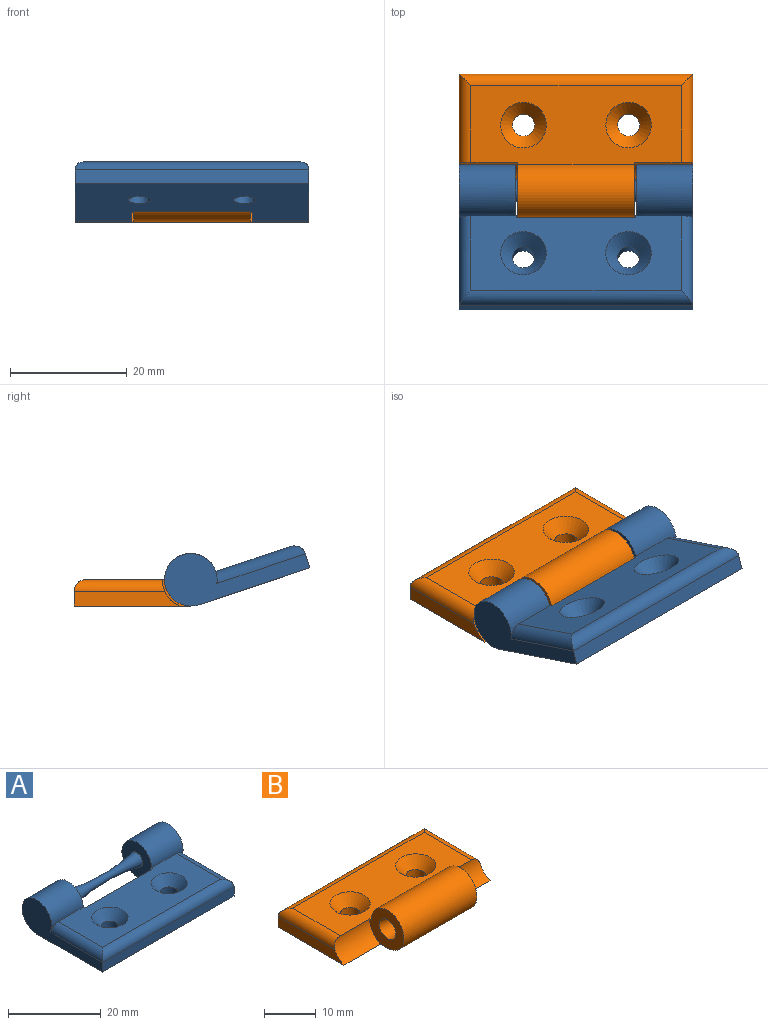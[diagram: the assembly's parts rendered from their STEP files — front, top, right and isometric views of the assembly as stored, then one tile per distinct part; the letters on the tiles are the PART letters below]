
ASSEMBLY  parts=2 mates=1
PART A: 22 faces, bbox 73.1x37x34 mm
  f0: torus R=52.24mm, axis (-1,0,0), area 150.9mm2, adj f1,f5
  f1: plane 9x9mm, normal (-1,0,0), area 58.1mm2, adj f0,f2,f3,f8
  f2: cylinder r=4.5mm len=9.6mm, axis (1,0,0), area 204.4mm2, adj f1,f3,f4,f9,f16
  f3: plane 40x20mm, normal (0,0,-1), area 675.6mm2, adj f1,f2,f4,f5,f6,f7,f8,f10
  f4: plane 24.5x9mm, normal (1,0,0), area 106.4mm2, adj f2,f3,f14,f16
  f5: plane 9x9mm, normal (1,0,0), area 56.2mm2, adj f0,f3,f7,f11
  f6: plane 24.5x9mm, normal (-1,0,0), area 106.4mm2, adj f3,f7,f14,f15
  f7: cylinder r=4.5mm len=9.6mm, axis (-1,0,0), area 204.4mm2, adj f3,f5,f6,f9,f15
  f8: plane 4.5x0.2mm, normal (0,1,0), area 0.9mm2, adj f1,f3,f9,f10
  f9: plane 36x13.5mm, normal (0,0,1), area 382.3mm2, adj f2,f7,f8,f10,f11,f12,f13,f15
  f10: plane 4.5x0.4mm, normal (-1,0,0), area 1.8mm2, adj f3,f8,f9,f13
  f11: plane 4.5x0.2mm, normal (0,1,0), area 0.9mm2, adj f3,f5,f9,f12
  f12: plane 4.5x0.4mm, normal (1,0,0), area 1.8mm2, adj f3,f9,f11,f13
  f13: plane 20.4x4.5mm, normal (0,1,0), area 91.8mm2, adj f3,f9,f10,f12
  f14: plane 40x2.5mm, normal (0,-1,0), area 100mm2, adj f3,f4,f6,f17
  f15: cylinder r=2mm len=15.97mm, axis (0,1,0), area 46.7mm2, adj f6,f7,f9,f17
  f16: cylinder r=2mm len=15.97mm, axis (0,-1,0), area 46.7mm2, adj f2,f4,f9,f17
  f17: cylinder r=2mm len=40mm, axis (-1,0,0), area 121.1mm2, adj f9,f14,f15,f16
  f18: cylinder r=1.9mm len=3.8mm, axis (0,0,1), area 26.2mm2, adj f3,f19
  f19: cone r=1.9mm half-angle=41deg, axis (0,0,1), area 55.5mm2, adj f9,f18
  f20: cylinder r=1.9mm len=3.8mm, axis (0,0,1), area 26.2mm2, adj f3,f21
  f21: cone r=1.9mm half-angle=41deg, axis (0,0,1), area 55.5mm2, adj f9,f20
PART B: 18 faces, bbox 72.5x37.3x34.6 mm
  f0: plane 9.4x9mm, normal (1,0,0), area 52.1mm2, adj f2,f3,f4,f6,f10
  f1: plane 9.4x9mm, normal (-1,0,0), area 50mm2, adj f2,f3,f4,f6,f8
  f2: cylinder r=4.5mm len=20mm, axis (-1,0,0), area 424.1mm2, adj f0,f1,f4,f6
  f3: torus R=52.24mm, axis (-1,0,0), area 192.6mm2, adj f0,f1
  f4: plane 40x20mm, normal (0,0,-1), area 738.6mm2, adj f0,f1,f2,f5,f7,f8,f9,f10
  f5: plane 40x2.5mm, normal (0,1,0), area 100mm2, adj f4,f7,f9,f12
  f6: plane 36x13.5mm, normal (0,0,1), area 384.1mm2, adj f0,f1,f2,f8,f10,f11,f12,f13
  f7: plane 18.06x2.5mm, normal (-1,0,0), area 41.2mm2, adj f4,f5,f8,f11
  f8: cylinder r=4.9mm len=10mm, axis (1,0,0), area 56.2mm2, adj f1,f4,f6,f7,f11
  f9: plane 18.06x2.5mm, normal (1,0,0), area 41.2mm2, adj f4,f5,f10,f13
  f10: cylinder r=4.9mm len=10mm, axis (-1,0,0), area 56.2mm2, adj f0,f4,f6,f9,f13
  f11: cylinder r=2mm len=15.53mm, axis (0,-1,0), area 45.5mm2, adj f6,f7,f8,f12
  f12: cylinder r=2mm len=40mm, axis (1,0,0), area 121.1mm2, adj f5,f6,f11,f13
  f13: cylinder r=2mm len=15.53mm, axis (0,-1,0), area 45.5mm2, adj f6,f9,f10,f12
  f14: cylinder r=1.9mm len=3.8mm, axis (0,0,1), area 26.2mm2, adj f4,f15
  f15: cone r=1.9mm half-angle=41deg, axis (0,0,1), area 55.5mm2, adj f6,f14
  f16: cylinder r=1.9mm len=3.8mm, axis (0,0,1), area 26.2mm2, adj f4,f17
  f17: cone r=1.9mm half-angle=41deg, axis (0,0,1), area 55.5mm2, adj f6,f16
PLACE A rot(axis=(-1,0,0),18.4deg) t=(-0.01,0,0)mm
PLACE B at identity fixed
MATE revolute A.f0 <-> B.f2  axis (1,0,0) through (19.99,0,0)mm
